# Revit family: Lighting - Current - Slide Post Top1
name_source: partatom
category: Lighting Fixtures
units: mm (PartAtom-declared; Revit-internal decimal feet)

## family parameters
Cut with Voids When Loaded = No
Host = Face
Light Source = Yes
OmniClass Number = 23.80.70.14
OmniClass Title = Luminaries for External Lighting
Part Type = Normal
Room Calculation Point = No
Round Connector Dimension = Use Diameter
Shared = No

## types (1)
- Lighting - Current - Slide Post Top1
    Apparent Load = 9 VA
    Assembly Code = D5020200
    Color Filter = 16777215
    Controller = Please Refer to the Product Spec Sheet for Control Options
    Default Elevation = 48 "
    Description = Slide Post top offers a more traditional look while maintaining modern curves and lines. Slide offers superior optical control the post top mount can even replace less visually appealing area mounting fixtures as it maintains great optical control.
    Dimmimng Protocol = 0-10V, 10%-100%, Dusk to Dawn, Scheduling
    Dimming Lamp Color Temperature Shift = <None>
    Features = Contemporary Post Top featuring clean lines for retail, courtyard, or hospitality applications
3 different shade options (flat, straight, or curve) as well as the ability to have no shade without affecting the performance
A set of three rings can be included on any luminaire configuration to add visual interest or block direct view of LEDs
Choice of 2 or 4 struts to customize based on the application preference
Slide has been designed to offer configurations with or without a lens
Post top mounts on 2 3/8” to 3” tenon
NX Lighting controls available
    Housing Material = Paint - Current - Black
    Installation and Service URL = https://cdn.currentlighting.com
    LED = LED - Current -  Yellow
    Lamp = LED
    Lens = Yes
    Lens Material = Glass - Current - Transparent
    Load Classification = Lighting
    Manufacturer = Current Lighting
    Model = Slide - Post Top
    Mounting = Please Refer to the Product Spec Sheet for Mounting Options
    Photometric Web File = SLD2-PT-4S-NL-80L-110-5K7-5QW-XXX.ies
    Photometry Note = Please load ies file listed under Photometric Web File for accurate rendering.
    Power Factor = 0.9
    Product Documentation Link = https://cdn.currentlighting.com
    Product Page URL = https://www.currentlighting.com
    Tilt Angle = 90.00°
    Type Comments = Light Fixture
    URL = https://www.currentlighting.com
    Voltage = 277 V
    Voltage Comments = 120-277V
    Wattage Comments = 25-112 W

## geometry (parser evidence)
native form markers: Sweep x2
no freeform markers — native parametric forms only
